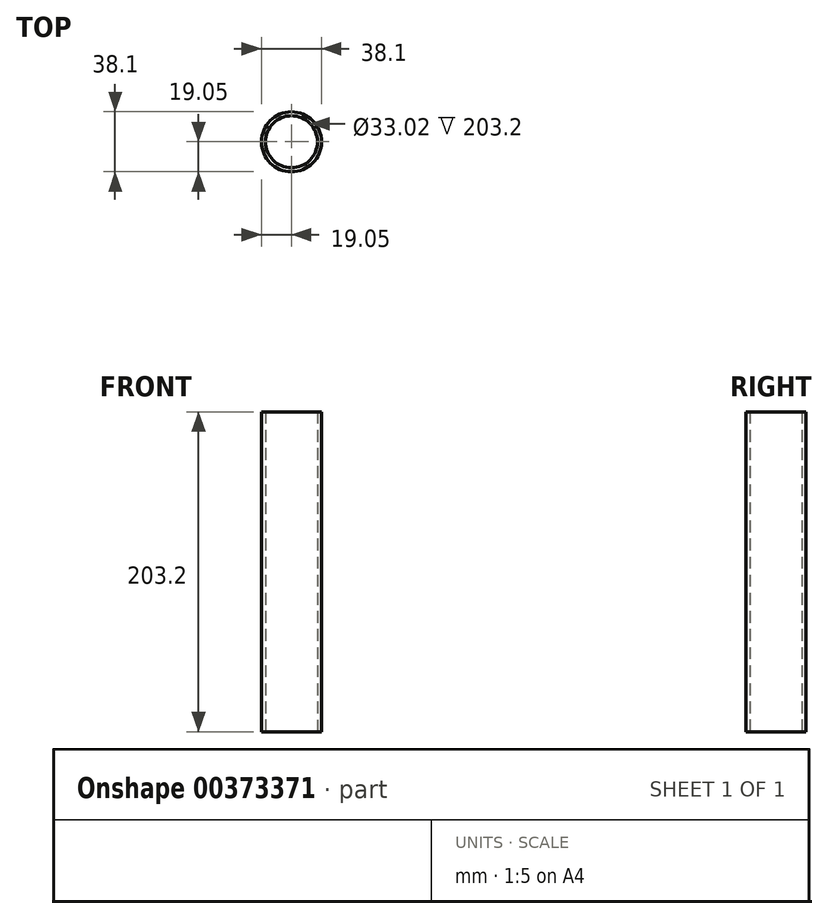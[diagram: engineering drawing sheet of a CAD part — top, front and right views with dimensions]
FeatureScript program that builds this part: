
annotation { "Feature Type Name" : "Feature", "Feature Type Description" : "" }
export const myFeature = defineFeature(function(context is Context, id is Id, definition is map)
    precondition{}
    {
        {
            var Q0;
            Q0=qCreatedBy(makeId("Top.planeOp"),FACE);
            var sketch = newSketch(context, id + "F0", { "sketchPlane" : qUnion([Q0])});
            skCircle(sketch, "E0", {"center": v(0, 0) * mm, "radius": 19.05 * mm});
            skCircle(sketch, "E1", {"center": v(0, 0) * mm, "radius": 16.51 * mm});
            skSolve(sketch);
        }
        {
            var Q0;
            Q0=makeQuery(id+"F0.imprint","IMPRINT",FACE,{"disambiguationData":[TD([[makeQuery(id+"F0.imprint","IMPRINT",EDGE,{"derivedFrom":sQuery(id+"F0.wireOp",EDGE,"E0")}),1.0]])]});
            extrude(context, id + "F1", {"entities" : qUnion([Q0]), "depth" : 203.2 * mm});
        }
    });
